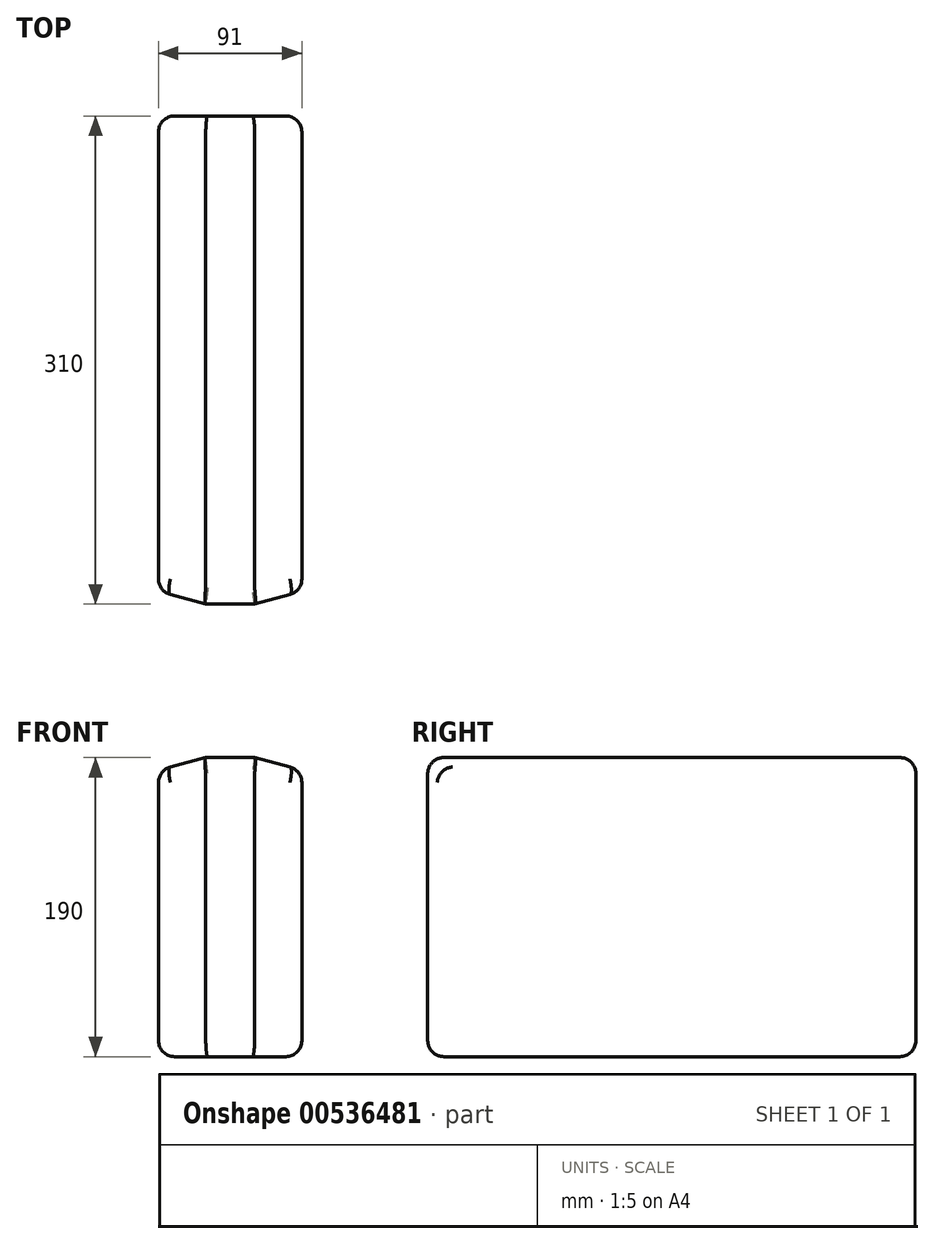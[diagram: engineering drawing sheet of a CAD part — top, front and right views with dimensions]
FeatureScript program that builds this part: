
annotation { "Feature Type Name" : "Feature", "Feature Type Description" : "" }
export const myFeature = defineFeature(function(context is Context, id is Id, definition is map)
    precondition{}
    {
        {
            var Q0;
            Q0=qCreatedBy(makeId("Top.planeOp"),FACE);
            var sketch = newSketch(context, id + "F0", { "sketchPlane" : qUnion([Q0])});
            skLineSegment(sketch, "E0.bottom", {"start": v(0, 0) * mm, "end": v(91, 0) * mm});
            skLineSegment(sketch, "E0.top", {"start": v(0, -310) * mm, "end": v(91, -310) * mm});
            skLineSegment(sketch, "E0.left", {"start": v(0, 0) * mm, "end": v(0, -310) * mm});
            skLineSegment(sketch, "E0.right", {"start": v(91, 0) * mm, "end": v(91, -310) * mm});
            skSolve(sketch);
        }
        {
            var Q0;
            Q0=makeQuery(id+"F0.imprint","IMPRINT",FACE,{"disambiguationData":[TD([[makeQuery(id+"F0.imprint","IMPRINT",EDGE,{"derivedFrom":sQuery(id+"F0.wireOp",EDGE,"E0.bottom")}),-1.0]])]});
            extrude(context, id + "F1", {"entities" : qUnion([Q0]), "depth" : 190 * mm, "offsetDistance" : 25.4 * mm});
        }
        {
            var Q0;
            Q0=makeQuery(id+"F1.opExtrude","SWEPT_EDGE",EDGE,{"disambiguationData":[OSD([sQuery(id+"F0.wireOp",EDGE,"E0.top"),sQuery(id+"F0.wireOp",EDGE,"E0.right")])]});
            var Q1;
            Q1=makeQuery(id+"F1.opExtrude","SWEPT_EDGE",EDGE,{"disambiguationData":[OSD([sQuery(id+"F0.wireOp",EDGE,"E0.top"),sQuery(id+"F0.wireOp",EDGE,"E0.left")])]});
            chamfer(context, id + "F2", {"entities" : qUnion([Q0, Q1]), "chamferType" : ChamferType.TWO_OFFSETS, "width1" : 8 * mm, "oppositeDirection" : false, "width2" : 30 * mm, "tangentPropagation" : true});
        }
        {
            var Q0;
            Q0=makeQuery(id+"F1.opExtrude","CAP_EDGE",EDGE,{"disambiguationData":[OSD([sQuery(id+"F0.wireOp",EDGE,"E0.right")])],"isStart":false});
            var Q1;
            Q1=makeQuery(id+"F1.opExtrude","CAP_EDGE",EDGE,{"disambiguationData":[OSD([sQuery(id+"F0.wireOp",EDGE,"E0.left")])],"isStart":false});
            chamfer(context, id + "F3", {"entities" : qUnion([Q0, Q1]), "chamferType" : ChamferType.TWO_OFFSETS, "width1" : 8 * mm, "oppositeDirection" : false, "width2" : 30 * mm, "tangentPropagation" : true});
        }
        {
            var Q0;
            Q0=makeQuery(id+"F1.opExtrude","SWEPT_FACE",FACE,{"disambiguationData":[OSD([sQuery(id+"F0.wireOp",EDGE,"E0.left")])]});
            var Q1;
            Q1=makeQuery(id+"F1.opExtrude","SWEPT_FACE",FACE,{"disambiguationData":[OSD([sQuery(id+"F0.wireOp",EDGE,"E0.right")])]});
            var Q2;
            Q2=makeQuery(id+"F1.opExtrude","CAP_FACE",FACE,{"disambiguationData":[OSD([sQuery(id+"F0.wireOp",EDGE,"E0.bottom"),sQuery(id+"F0.wireOp",EDGE,"E0.top"),sQuery(id+"F0.wireOp",EDGE,"E0.left"),sQuery(id+"F0.wireOp",EDGE,"E0.right")])],"isStart":true});
            var Q3;
            {var subQ0=sQuery(id+"F0.wireOp",EDGE,"E0.right");Q3=makeQuery(id+"F3.opChamfer","BLEND_EDGE",EDGE,{"blendedFrom":[makeQuery(id+"F1.opExtrude","CAP_EDGE",EDGE,{"disambiguationData":[OSD([subQ0])],"isStart":false}),makeQuery(id+"F2.opChamfer","BLEND_FACE",FACE,{"disambiguationData":[OSD([sQuery(id+"F0.wireOp",EDGE,"E0.top"),subQ0])]})],"blendedInto":[makeQuery(id+"F2.opChamfer","BLEND_FACE",FACE,{"disambiguationData":[OSD([sQuery(id+"F0.wireOp",EDGE,"E0.top"),subQ0])]})]});}
            var Q4;
            Q4=makeQuery(id+"F1.opExtrude","CAP_EDGE",EDGE,{"disambiguationData":[OSD([sQuery(id+"F0.wireOp",EDGE,"E0.top")])],"isStart":false});
            var Q5;
            {var subQ0=sQuery(id+"F0.wireOp",EDGE,"E0.left");Q5=makeQuery(id+"F3.opChamfer","BLEND_EDGE",EDGE,{"blendedFrom":[makeQuery(id+"F1.opExtrude","CAP_EDGE",EDGE,{"disambiguationData":[OSD([subQ0])],"isStart":false}),makeQuery(id+"F2.opChamfer","BLEND_FACE",FACE,{"disambiguationData":[OSD([sQuery(id+"F0.wireOp",EDGE,"E0.top"),subQ0])]})],"blendedInto":[makeQuery(id+"F2.opChamfer","BLEND_FACE",FACE,{"disambiguationData":[OSD([sQuery(id+"F0.wireOp",EDGE,"E0.top"),subQ0])]})]});}
            var Q6;
            Q6=makeQuery(id+"F3.opChamfer","BLEND_EDGE",EDGE,{"blendedFrom":[makeQuery(id+"F1.opExtrude","CAP_EDGE",EDGE,{"disambiguationData":[OSD([sQuery(id+"F0.wireOp",EDGE,"E0.left")])],"isStart":false}),makeQuery(id+"F1.opExtrude","SWEPT_FACE",FACE,{"disambiguationData":[OSD([sQuery(id+"F0.wireOp",EDGE,"E0.bottom")])]})],"blendedInto":[makeQuery(id+"F1.opExtrude","SWEPT_FACE",FACE,{"disambiguationData":[OSD([sQuery(id+"F0.wireOp",EDGE,"E0.bottom")])]})]});
            var Q7;
            Q7=makeQuery(id+"F3.opChamfer","BLEND_EDGE",EDGE,{"blendedFrom":[makeQuery(id+"F1.opExtrude","CAP_EDGE",EDGE,{"disambiguationData":[OSD([sQuery(id+"F0.wireOp",EDGE,"E0.right")])],"isStart":false}),makeQuery(id+"F1.opExtrude","SWEPT_FACE",FACE,{"disambiguationData":[OSD([sQuery(id+"F0.wireOp",EDGE,"E0.bottom")])]})],"blendedInto":[makeQuery(id+"F1.opExtrude","SWEPT_FACE",FACE,{"disambiguationData":[OSD([sQuery(id+"F0.wireOp",EDGE,"E0.bottom")])]})]});
            var Q8;
            Q8=makeQuery(id+"F1.opExtrude","CAP_EDGE",EDGE,{"disambiguationData":[OSD([sQuery(id+"F0.wireOp",EDGE,"E0.bottom")])],"isStart":false});
            fillet(context, id + "F4", {"entities" : qUnion([Q0, Q1, Q2, Q3, Q4, Q5, Q6, Q7, Q8]), "radius" : 10.16 * mm, "tangentPropagation" : true, "allowEdgeOverflow" : false});
        }
    });
